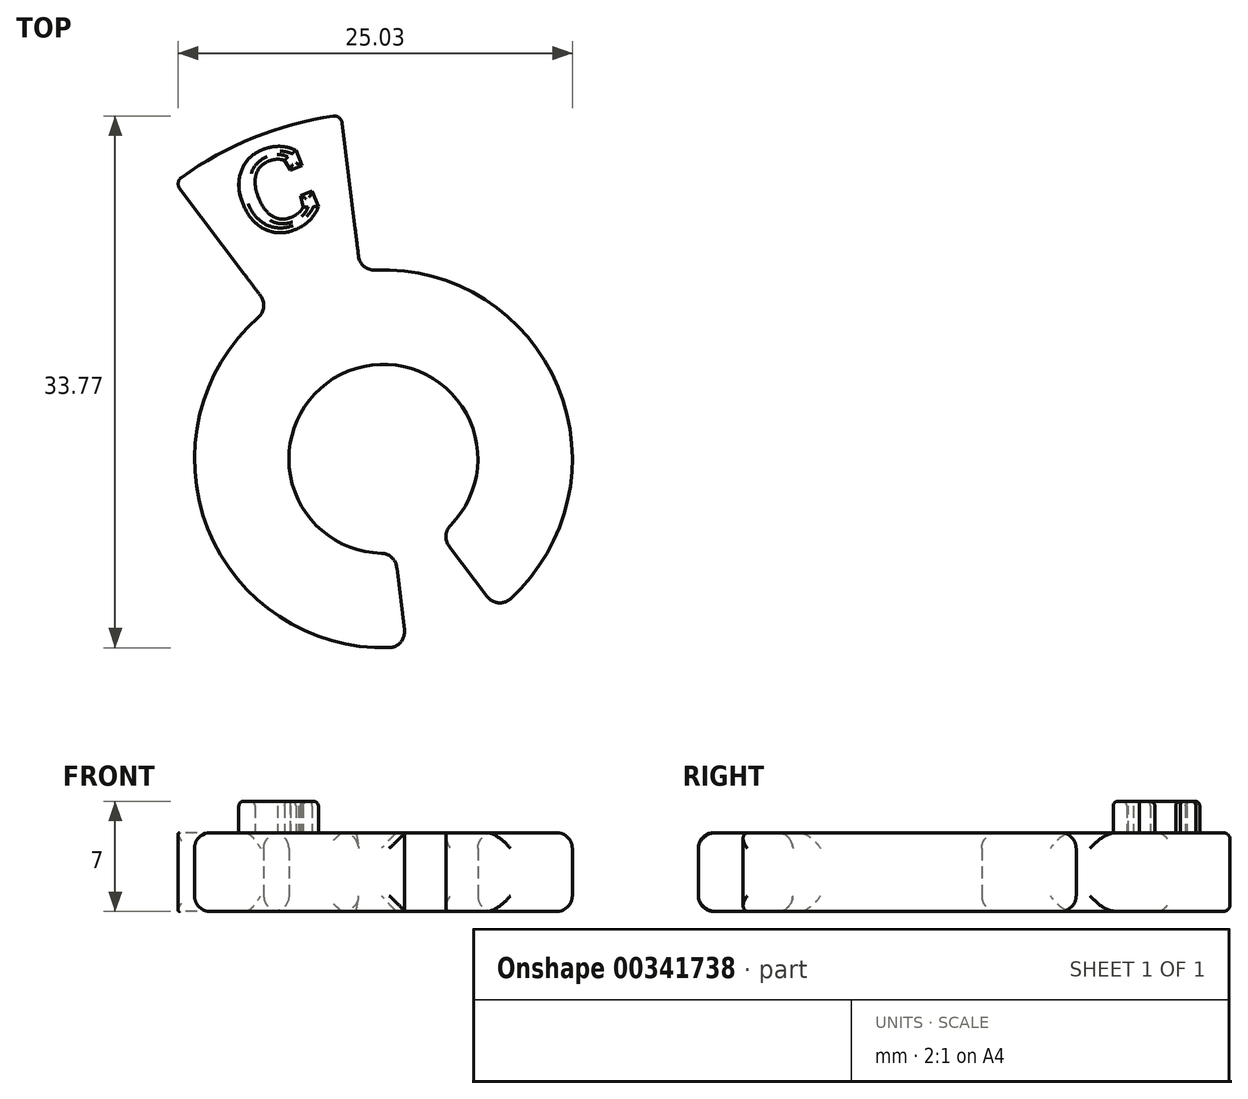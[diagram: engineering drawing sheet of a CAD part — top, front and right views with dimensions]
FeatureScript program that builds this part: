
annotation { "Feature Type Name" : "Feature", "Feature Type Description" : "" }
export const myFeature = defineFeature(function(context is Context, id is Id, definition is map)
    precondition{}
    {
        {
            var Q0;
            Q0=qCreatedBy(makeId("Top.planeOp"),FACE);
            var sketch = newSketch(context, id + "F0", { "sketchPlane" : qUnion([Q0])});
            skCircle(sketch, "E0", {"center": v(0, 0) * mm, "radius": 6 * mm});
            skCircle(sketch, "E1", {"center": v(0, 0) * mm, "radius": 12 * mm});
            skLineSegment(sketch, "E2", {"start": v(0, 0) * mm, "end": v(7.22, -9.58) * mm});
            skLineSegment(sketch, "E3", {"start": v(0, 0) * mm, "end": v(1.46, -11.91) * mm});
            skLineSegment(sketch, "E4", {"start": v(0, 0) * mm, "end": v(-2.68, 21.84) * mm});
            skLineSegment(sketch, "E5", {"start": v(0, 0) * mm, "end": v(-13.24, 17.57) * mm});
            skArc(sketch, "E6", {"start": v(-2.68, 21.84) * mm, "mid": v(-8.24, 20.4) * mm, "end": v(-13.24, 17.57) * mm});
            skSolve(sketch);
        }
        {
            var Q0;
            {var subQ0=sQuery(id+"F0.wireOp",EDGE,"E2");var subQ1=sQuery(id+"F0.wireOp",EDGE,"E0");var subQ2=makeQuery(id+"F0.imprint","INTERSECT",VERTEX,{"derivedFrom":[subQ1,subQ0]});Q0=makeQuery(id+"F0.imprint","IMPRINT",FACE,{"disambiguationData":[TD([[makeQuery(id+"F0.imprint","IMPRINT",EDGE,{"disambiguationData":[TD([[subQ2,-1.0]])],"derivedFrom":subQ1}),-1.0]])]});}
            var Q1;
            {var subQ0=sQuery(id+"F0.wireOp",EDGE,"E5");var subQ1=sQuery(id+"F0.wireOp",EDGE,"E0");var subQ2=makeQuery(id+"F0.imprint","INTERSECT",VERTEX,{"derivedFrom":[subQ1,subQ0]});Q1=makeQuery(id+"F0.imprint","IMPRINT",FACE,{"disambiguationData":[TD([[makeQuery(id+"F0.imprint","IMPRINT",EDGE,{"disambiguationData":[TD([[subQ2,-1.0]])],"derivedFrom":subQ1}),-1.0]])]});}
            var Q2;
            {var subQ0=sQuery(id+"F0.wireOp",EDGE,"E5");var subQ1=sQuery(id+"F0.wireOp",EDGE,"E0");var subQ2=makeQuery(id+"F0.imprint","INTERSECT",VERTEX,{"derivedFrom":[subQ1,subQ0]});Q2=makeQuery(id+"F0.imprint","IMPRINT",FACE,{"disambiguationData":[TD([[makeQuery(id+"F0.imprint","IMPRINT",EDGE,{"disambiguationData":[TD([[subQ2,1.0]])],"derivedFrom":subQ1}),-1.0]])]});}
            var Q3;
            {var subQ5=sQuery(id+"F0.wireOp",EDGE,"E6");Q3=makeQuery(id+"F0.imprint","IMPRINT",FACE,{"disambiguationData":[TD([[makeQuery(id+"F0.imprint","IMPRINT",EDGE,{"derivedFrom":subQ5}),1.0]])]});}
            extrude(context, id + "F1", {"entities" : qUnion([Q0, Q1, Q2, Q3]), "depth" : 5 * mm});
        }
        {
            var Q0;
            Q0=makeQuery(id+"F1.opExtrude","SWEPT_FACE",FACE,{"disambiguationData":[OSD([sQuery(id+"F0.wireOp",EDGE,"E1")])]});
            var Q1;
            Q1=makeQuery(id+"F1.opExtrude","SWEPT_FACE",FACE,{"disambiguationData":[OSD([sQuery(id+"F0.wireOp",EDGE,"E0")])]});
            fillet(context, id + "F2", {"entities" : qUnion([Q0, Q1]), "radius" : 1 * mm, "tangentPropagation" : true, "allowEdgeOverflow" : false});
        }
        {
            var Q0;
            Q0=makeQuery(id+"F1.opExtrude","CAP_FACE",FACE,{"disambiguationData":[OSD([sQuery(id+"F0.wireOp",EDGE,"E0"),sQuery(id+"F0.wireOp",EDGE,"E1"),sQuery(id+"F0.wireOp",EDGE,"E2"),sQuery(id+"F0.wireOp",EDGE,"E3"),sQuery(id+"F0.wireOp",EDGE,"E4"),sQuery(id+"F0.wireOp",EDGE,"E5"),sQuery(id+"F0.wireOp",EDGE,"E6")])],"isStart":false});
            var sketch = newSketch(context, id + "F3", { "sketchPlane" : qUnion([Q0])});
            skText(sketch, "E7", { "text": "C", "fontName": "RobotoSlab-Bold.ttf"});
            const initialGuessF3  = {"E7": [-0.0081, 0.01364, 0.92844, 0.37147, 0.0054]};
            skSetInitialGuess(sketch, initialGuessF3);
            skSolve(sketch);
        }
        {
            var Q0;
            Q0=makeQuery(id+"F3.imprint","IMPRINT",FACE,{"disambiguationData":[TD([[makeQuery(id+"F3.imprint","IMPRINT",EDGE,{"derivedFrom":sQuery(id+"F3.wireOp",EDGE,"E7.sketch_text.stroke-0")}),-1.0]])]});
            extrude(context, id + "F4", {"entities" : qUnion([Q0]), "operationType" : NewBodyOperationType.ADD, "depth" : 2 * mm});
        }
        {
            var Q0;
            Q0=makeQuery(id+"F4.opExtrude","CAP_FACE",FACE,{"disambiguationData":[OSD([sQuery(id+"F3.wireOp",EDGE,"E7.sketch_text.stroke-0"),sQuery(id+"F3.wireOp",EDGE,"E7.sketch_text.stroke-1"),sQuery(id+"F3.wireOp",EDGE,"E7.sketch_text.stroke-2"),sQuery(id+"F3.wireOp",EDGE,"E7.sketch_text.stroke-3"),sQuery(id+"F3.wireOp",EDGE,"E7.sketch_text.stroke-4"),sQuery(id+"F3.wireOp",EDGE,"E7.sketch_text.stroke-5"),sQuery(id+"F3.wireOp",EDGE,"E7.sketch_text.stroke-6"),sQuery(id+"F3.wireOp",EDGE,"E7.sketch_text.stroke-7"),sQuery(id+"F3.wireOp",EDGE,"E7.sketch_text.stroke-8"),sQuery(id+"F3.wireOp",EDGE,"E7.sketch_text.stroke-9"),sQuery(id+"F3.wireOp",EDGE,"E7.sketch_text.stroke-10"),sQuery(id+"F3.wireOp",EDGE,"E7.sketch_text.stroke-11"),sQuery(id+"F3.wireOp",EDGE,"E7.sketch_text.stroke-12"),sQuery(id+"F3.wireOp",EDGE,"E7.sketch_text.stroke-13"),sQuery(id+"F3.wireOp",EDGE,"E7.sketch_text.stroke-14"),sQuery(id+"F3.wireOp",EDGE,"E7.sketch_text.stroke-15"),sQuery(id+"F3.wireOp",EDGE,"E7.sketch_text.stroke-16"),sQuery(id+"F3.wireOp",EDGE,"E7.sketch_text.stroke-17"),sQuery(id+"F3.wireOp",EDGE,"E7.sketch_text.stroke-18"),sQuery(id+"F3.wireOp",EDGE,"E7.sketch_text.stroke-19"),sQuery(id+"F3.wireOp",EDGE,"E7.sketch_text.stroke-20"),sQuery(id+"F3.wireOp",EDGE,"E7.sketch_text.stroke-21"),sQuery(id+"F3.wireOp",EDGE,"E7.sketch_text.stroke-22"),sQuery(id+"F3.wireOp",EDGE,"E7.sketch_text.stroke-23")])],"isStart":false});
            fillet(context, id + "F5", {"entities" : qUnion([Q0]), "radius" : 0.3 * mm, "tangentPropagation" : true, "allowEdgeOverflow" : false});
        }
        {
            var Q0;
            Q0=makeQuery(id+"F1.opExtrude","SWEPT_FACE",FACE,{"disambiguationData":[OSD([sQuery(id+"F0.wireOp",EDGE,"E6")])]});
            fillet(context, id + "F6", {"entities" : qUnion([Q0]), "radius" : 0.5 * mm, "tangentPropagation" : true, "allowEdgeOverflow" : false});
        }
    });
